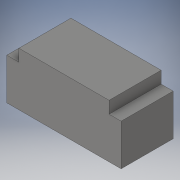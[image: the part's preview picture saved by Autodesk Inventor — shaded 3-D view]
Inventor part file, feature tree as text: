
AUTODESK INVENTOR PART (.ipt)
format: ipt  version: 2019 (Build 230136000, 136)  size: 108,544 bytes
history: native  units: mm
features: other x7, extrude x1, sketch x1
ambient origin geometry x8: Origin, YZ Plane, XZ Plane, XY Plane, X Axis, Y Axis, Z Axis, Center Point
bodies: Solid1 (feature_tree)
feature tree (9):
  extrude  "Extrusion1"  TaperAngle=0.0deg  [1 undecoded]
  other  "p1_XY"
  other  "p1_YZ"
  other  "p1_ZX"
  other  "p1_X"
  other  "p1_Y"
  other  "p1_Z"
  other  "p1_Center"
  sketch  "Sketch_1"  dims[d0=8.2mm d1=0.0mm d2=0.0mm]
note: 1 required parameter value undecoded (feature->parameter linkage not recoverable at this tier; creation-order binding heuristic only, values carry confidence <= 0.55)
